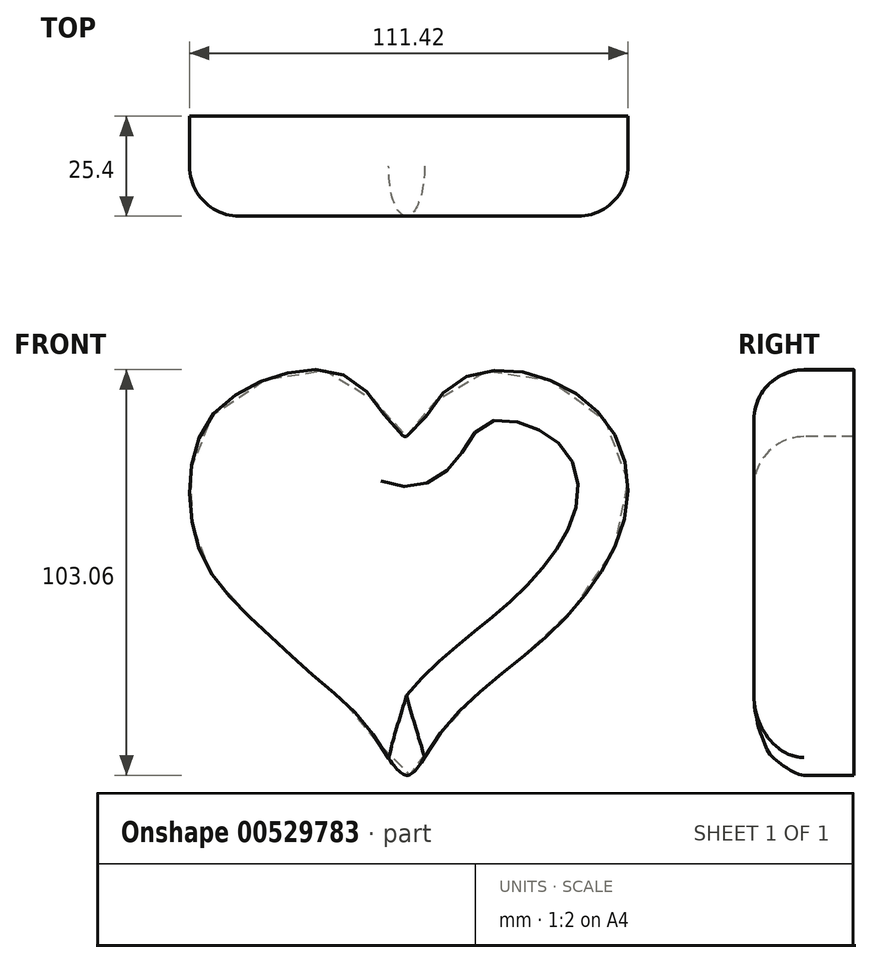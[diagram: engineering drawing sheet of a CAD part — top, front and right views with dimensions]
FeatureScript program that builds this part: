
annotation { "Feature Type Name" : "Feature", "Feature Type Description" : "" }
export const myFeature = defineFeature(function(context is Context, id is Id, definition is map)
    precondition{}
    {
        {
            var Q0;
            Q0=qCreatedBy(makeId("Front.planeOp"),FACE);
            var sketch = newSketch(context, id + "F0", { "sketchPlane" : qUnion([Q0])});
            skFitSpline(sketch, "E0", {"points": [v(0, 40.5) * mm, v(9.3, 51.7) * mm, v(28.63, 57.03) * mm, v(51.05, 43.86) * mm, v(55.13, 18.64) * mm, v(37.88, -7.99) * mm, v(19.38, -23.68) * mm, v(6.77, -37.41) * mm, v(-0.02, -45.54) * mm, v(-8.64, -34.9) * mm, v(-21.54, -22) * mm, v(-41.71, -3.5) * mm, v(-51.8, 9.67) * mm, v(-55.17, 26.76) * mm, v(-49.32, 46) * mm, v(-28.45, 57.03) * mm, v(-11.2, 52.95) * mm, v(0, 40.5) * mm]});
            skSolve(sketch);
        }
        {
            var Q0;
            Q0 = qSketchRegion(id + "F0", true);
            extrude(context, id + "F1", {"entities" : qUnion([Q0]), "depth" : 25.4 * mm, "offsetDistance" : 25.4 * mm});
        }
        {
            var Q0;
            Q0=makeQuery(id+"F1.opExtrude","CAP_FACE",FACE,{"disambiguationData":[OSD([sQuery(id+"F0.wireOp",EDGE,"E0")])],"isStart":false});
            fillet(context, id + "F2", {"entities" : qUnion([Q0]), "radius" : 12.7 * mm, "tangentPropagation" : true, "allowEdgeOverflow" : false});
        }
    });
